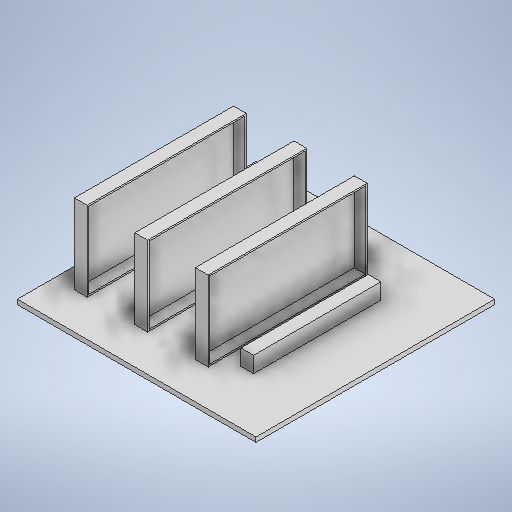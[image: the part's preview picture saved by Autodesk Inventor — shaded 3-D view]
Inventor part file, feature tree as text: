
AUTODESK INVENTOR PART (.ipt)
format: ipt  version: 2025.2 (Build 292293000, 293)  size: 306,688 bytes
history: native  units: mm
features: extrude x3, other x1, sketch x1, shell x1
ambient origin geometry x8: Origin, YZ Plane, XZ Plane, XY Plane, X Axis, Y Axis, Z Axis, Center Point
bodies: Body1 (feature_tree)
feature tree (6):
  other  "Sólido1"
  sketch  "Esboço1"  dims[d0=150.0mm d1=150.0mm d15=3.0mm d16=0.0mm d17=50.0mm d18=0.0mm d19=10.0mm d20=0.0mm d21=1.0mm]
  extrude  "Extrusão1"  Depth=150.0mm
  extrude  "Extrusão2"  Depth=3.0mm TaperAngle=0.0deg
  extrude  "Extrusão3"  Depth=50.0mm TaperAngle=0.0deg
  shell  "Casca1"  Thickness=10.0mm
